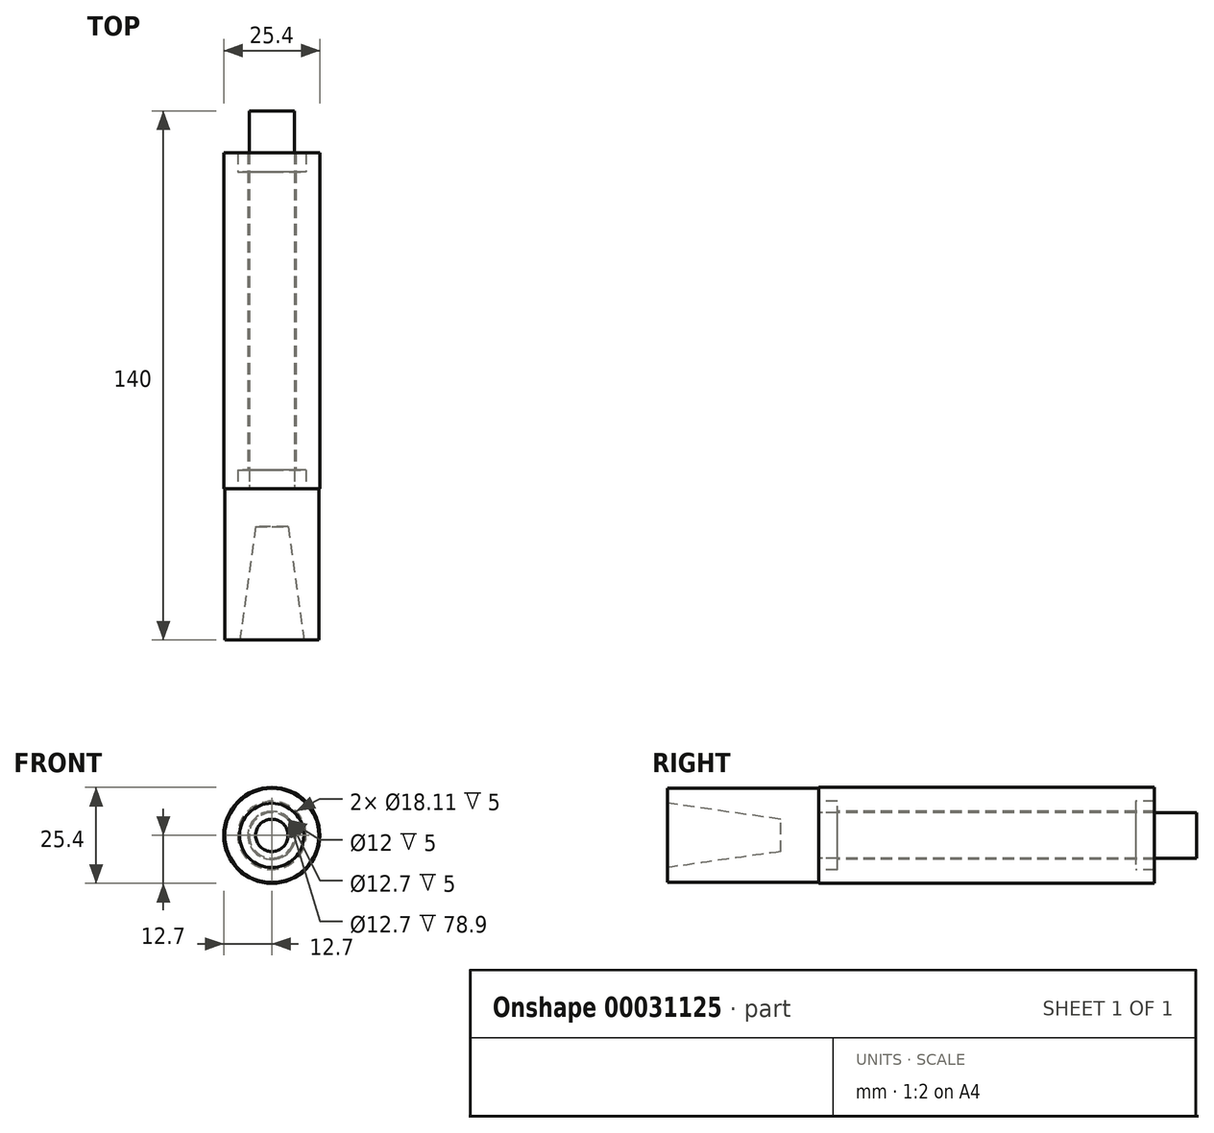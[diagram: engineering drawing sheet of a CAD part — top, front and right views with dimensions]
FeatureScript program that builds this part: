
annotation { "Feature Type Name" : "Feature", "Feature Type Description" : "" }
export const myFeature = defineFeature(function(context is Context, id is Id, definition is map)
    precondition{}
    {
        {
            var Q0;
            Q0=qCreatedBy(makeId("Front.planeOp"),FACE);
            var sketch = newSketch(context, id + "F0", { "sketchPlane" : qUnion([Q0])});
            skCircle(sketch, "E0", {"center": v(0, 0) * mm, "radius": 6 * mm});
            skCircle(sketch, "E1", {"center": v(0, 0) * mm, "radius": 9.06 * mm});
            skCircle(sketch, "E2", {"center": v(0, 0) * mm, "radius": 12.7 * mm});
            skCircle(sketch, "E3", {"center": v(0, 0) * mm, "radius": 12.45 * mm});
            skCircle(sketch, "E4", {"center": v(0, 0) * mm, "radius": 6.35 * mm});
            skSolve(sketch);
        }
        {
            var Q0;
            Q0=makeQuery(id+"F0.imprint","IMPRINT",FACE,{"disambiguationData":[TD([[makeQuery(id+"F0.imprint","IMPRINT",EDGE,{"derivedFrom":sQuery(id+"F0.wireOp",EDGE,"E0")}),1.0]])]});
            extrude(context, id + "F1", {"entities" : qUnion([Q0]), "oppositeDirection" : true, "depth" : 100 * mm});
        }
        {
            var Q0;
            Q0=makeQuery(id+"F0.imprint","IMPRINT",FACE,{"disambiguationData":[TD([[makeQuery(id+"F0.imprint","IMPRINT",EDGE,{"derivedFrom":sQuery(id+"F0.wireOp",EDGE,"E0")}),1.0]])]});
            var Q1;
            Q1=makeQuery(id+"F0.imprint","IMPRINT",FACE,{"disambiguationData":[TD([[makeQuery(id+"F0.imprint","IMPRINT",EDGE,{"derivedFrom":sQuery(id+"F0.wireOp",EDGE,"E1")}),1.0]])]});
            var Q2;
            Q2=makeQuery(id+"F0.imprint","IMPRINT",FACE,{"disambiguationData":[TD([[makeQuery(id+"F0.imprint","IMPRINT",EDGE,{"derivedFrom":sQuery(id+"F0.wireOp",EDGE,"E1")}),-1.0]])]});
            var Q3;
            Q3=makeQuery(id+"F0.imprint","IMPRINT",FACE,{"disambiguationData":[TD([[makeQuery(id+"F0.imprint","IMPRINT",EDGE,{"derivedFrom":sQuery(id+"F0.wireOp",EDGE,"E0")}),-1.0]])]});
            var Q4;
            Q4=makeQuery(id+"F0.imprint","IMPRINT",FACE,{"disambiguationData":[TD([[makeQuery(id+"F0.imprint","IMPRINT",EDGE,{"derivedFrom":sQuery(id+"F0.wireOp",EDGE,"E4")}),-1.0]])]});
            extrude(context, id + "F2", {"entities" : qUnion([Q0, Q1, Q2, Q3, Q4]), "operationType" : NewBodyOperationType.ADD, "depth" : 40 * mm});
        }
        {
            var Q0;
            Q0=makeQuery(id+"F2.opExtrude","CAP_FACE",FACE,{"disambiguationData":[OSD([sQuery(id+"F0.wireOp",EDGE,"E3")])],"isStart":false});
            var sketch = newSketch(context, id + "F3", { "sketchPlane" : qUnion([Q0])});
            skCircle(sketch, "E5", {"center": v(0, 0) * mm, "radius": 8.5 * mm});
            skSolve(sketch);
        }
        {
            var Q0;
            Q0=makeQuery(id+"F3.imprint","IMPRINT",FACE,{"disambiguationData":[TD([[makeQuery(id+"F3.imprint","IMPRINT",EDGE,{"derivedFrom":sQuery(id+"F3.wireOp",EDGE,"E5")}),1.0]])]});
            extrude(context, id + "F4", {"entities" : qUnion([Q0]), "operationType" : NewBodyOperationType.REMOVE, "oppositeDirection" : true, "depth" : 30 * mm, "hasDraft" : true, "draftAngle" : 8 * degree, "draftPullDirection" : true});
        }
        {
            var Q0;
            Q0=makeQuery(id+"F0.imprint","IMPRINT",FACE,{"disambiguationData":[TD([[makeQuery(id+"F0.imprint","IMPRINT",EDGE,{"derivedFrom":sQuery(id+"F0.wireOp",EDGE,"E1")}),-1.0]])]});
            var Q1;
            Q1=makeQuery(id+"F0.imprint","IMPRINT",FACE,{"disambiguationData":[TD([[makeQuery(id+"F0.imprint","IMPRINT",EDGE,{"derivedFrom":sQuery(id+"F0.wireOp",EDGE,"E2")}),1.0]])]});
            var Q2;
            Q2=makeQuery(id+"F0.imprint","IMPRINT",FACE,{"disambiguationData":[TD([[makeQuery(id+"F0.imprint","IMPRINT",EDGE,{"derivedFrom":sQuery(id+"F0.wireOp",EDGE,"E1")}),1.0]])]});
            extrude(context, id + "F5", {"entities" : qUnion([Q0, Q1, Q2]), "oppositeDirection" : true, "depth" : 88.9 * mm});
        }
        {
            var Q0;
            Q0=makeQuery(id+"F0.imprint","IMPRINT",FACE,{"disambiguationData":[TD([[makeQuery(id+"F0.imprint","IMPRINT",EDGE,{"derivedFrom":sQuery(id+"F0.wireOp",EDGE,"E1")}),1.0]])]});
            extrude(context, id + "F6", {"entities" : qUnion([Q0]), "operationType" : NewBodyOperationType.REMOVE, "oppositeDirection" : true, "depth" : 5 * mm});
        }
        {
            var Q0;
            Q0=makeQuery(id+"F0.imprint","IMPRINT",FACE,{"disambiguationData":[TD([[makeQuery(id+"F0.imprint","IMPRINT",EDGE,{"derivedFrom":sQuery(id+"F0.wireOp",EDGE,"E1")}),1.0]])]});
            var Q1;
            Q1=makeQuery(id+"F0.imprint","IMPRINT",FACE,{"disambiguationData":[TD([[makeQuery(id+"F0.imprint","IMPRINT",EDGE,{"derivedFrom":sQuery(id+"F0.wireOp",EDGE,"E0")}),-1.0]])]});
            extrude(context, id + "F7", {"entities" : qUnion([Q0, Q1]), "oppositeDirection" : true, "depth" : 5 * mm});
        }
        {
            var Q0;
            Q0=makeQuery(id+"F5.opExtrude","CAP_FACE",FACE,{"disambiguationData":[OSD([sQuery(id+"F0.wireOp",EDGE,"E2"),sQuery(id+"F0.wireOp",EDGE,"E4")])],"isStart":false});
            var sketch = newSketch(context, id + "F8", { "sketchPlane" : qUnion([Q0])});
            skCircle(sketch, "E6", {"center": v(0, 0) * mm, "radius": 9.06 * mm});
            skSolve(sketch);
        }
        {
            var Q0;
            Q0 = qSketchRegion(id + "F8", true);
            extrude(context, id + "F9", {"entities" : qUnion([Q0]), "operationType" : NewBodyOperationType.REMOVE, "oppositeDirection" : true, "depth" : 5 * mm});
        }
        {
            var Q0;
            Q0=makeQuery(id+"F9.boolean.opBoolean","COPY",FACE,{"derivedFrom":makeQuery(id+"F9.opExtrude","CAP_FACE",FACE,{"disambiguationData":[OSD([sQuery(id+"F8.wireOp",EDGE,"E6")])],"isStart":false})});
            extrude(context, id + "F10", {"entities" : qUnion([Q0]), "depth" : 5 * mm});
        }
    });
